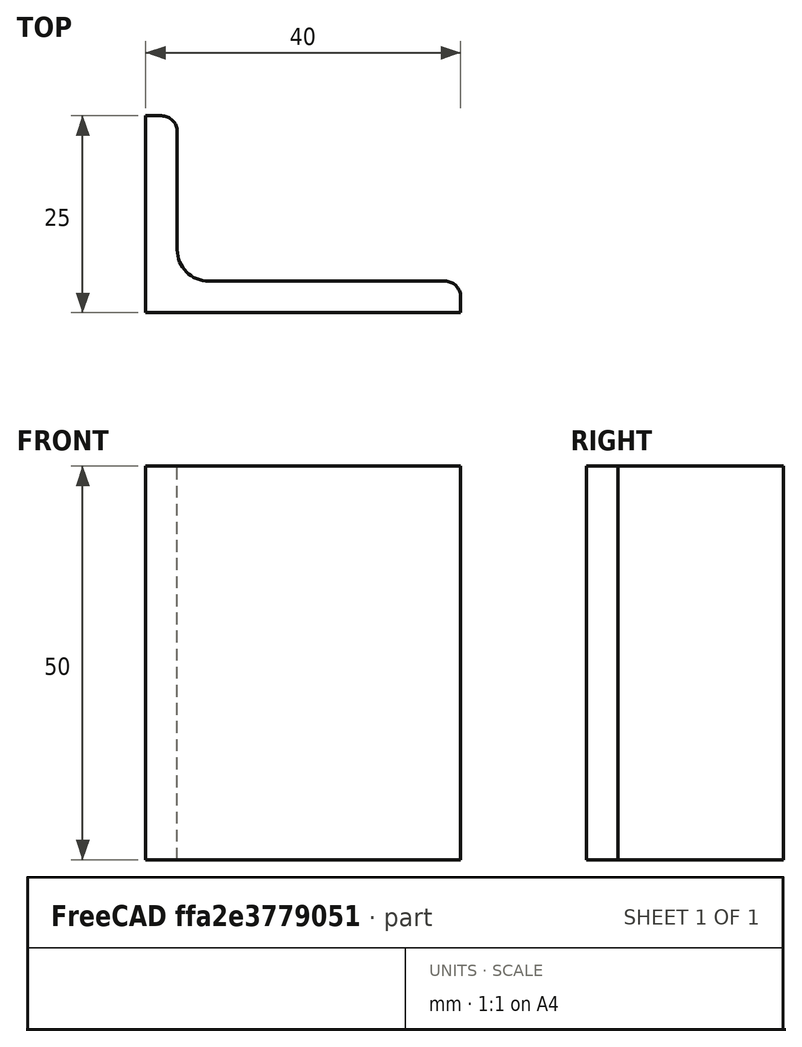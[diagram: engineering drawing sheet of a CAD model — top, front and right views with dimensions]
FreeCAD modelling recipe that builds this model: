
FCSTD DOCUMENT  (FreeCAD 0.15R4671 (Git))
Label: Angle Bar 40x25x4 EN10056 S235JR
License: All rights reserved
LicenseURL: http://en.wikipedia.org/wiki/All_rights_reserved
objects: Sketcher::SketchObject×1, Part::Extrusion×1
note: 2 computed .brp shape members not serialized (recipe doc carries the construction recipe); baked Part::Feature solids carry a one-line shape summary decoded from their .brp

FEATURE [Sketcher::SketchObject] Sketch
  sketch-geometry (9):
    g0: LineSegment StartX=0 StartY=0 StartZ=0 EndX=40 EndY=0 EndZ=0
    g1: LineSegment StartX=40 StartY=0 StartZ=0 EndX=40 EndY=2 EndZ=0
    g2: LineSegment StartX=38 StartY=4 StartZ=0 EndX=8 EndY=4 EndZ=0
    g3: LineSegment StartX=0 StartY=0 StartZ=0 EndX=0 EndY=25 EndZ=0
    g4: LineSegment StartX=0 StartY=25 StartZ=0 EndX=2 EndY=25 EndZ=0
    g5: LineSegment StartX=4 StartY=23 StartZ=0 EndX=4 EndY=8 EndZ=0
    g6: ArcOfCircle CenterX=8 CenterY=8 CenterZ=0 NormalX=0 NormalY=0 NormalZ=1 Radius=4 StartAngle=3.14159 EndAngle=4.71239
    g7: ArcOfCircle CenterX=2 CenterY=23 CenterZ=0 NormalX=0 NormalY=0 NormalZ=1 Radius=2 StartAngle=0 EndAngle=1.5708
    g8: ArcOfCircle CenterX=38 CenterY=2 CenterZ=0 NormalX=0 NormalY=0 NormalZ=1 Radius=2 StartAngle=0 EndAngle=1.5708
  constraints (23):
    c: Coincident(g0,g-1)
    c: Horizontal(g0)
    c: Coincident(g1,g0)
    c: Vertical(g1)
    c: Horizontal(g2)
    c: Coincident(g3,g-1)
    c: Vertical(g3)
    c: Coincident(g4,g3)
    c: Horizontal(g4)
    c: Vertical(g5)
    c: Tangent(g5,g6) = -1.5708
    c: Tangent(g2,g6) = 1.5708
    c: Tangent(g4,g7) = 1.5708
    c: Tangent(g5,g7) = 1.5708
    c: Tangent(g2,g8) = -1.5708
    c: Tangent(g1,g8) = -1.5708
    c: DistanceX(g0) = 40
    c: DistanceY(g3) = 25
    c: DistanceY(g0,g2) = 4
    c: DistanceX(g3,g5) = 4
    c: Radius(g6) = 4
    c: Radius(g8) = 2
    c: Radius(g7) = 2
FEATURE [Part::Extrusion] Extrude  label="Angle Bar 40x25x4 EN10056 S235JR"
  Base = -> Sketch
  Dir = (0,0,50)
  Solid = true
